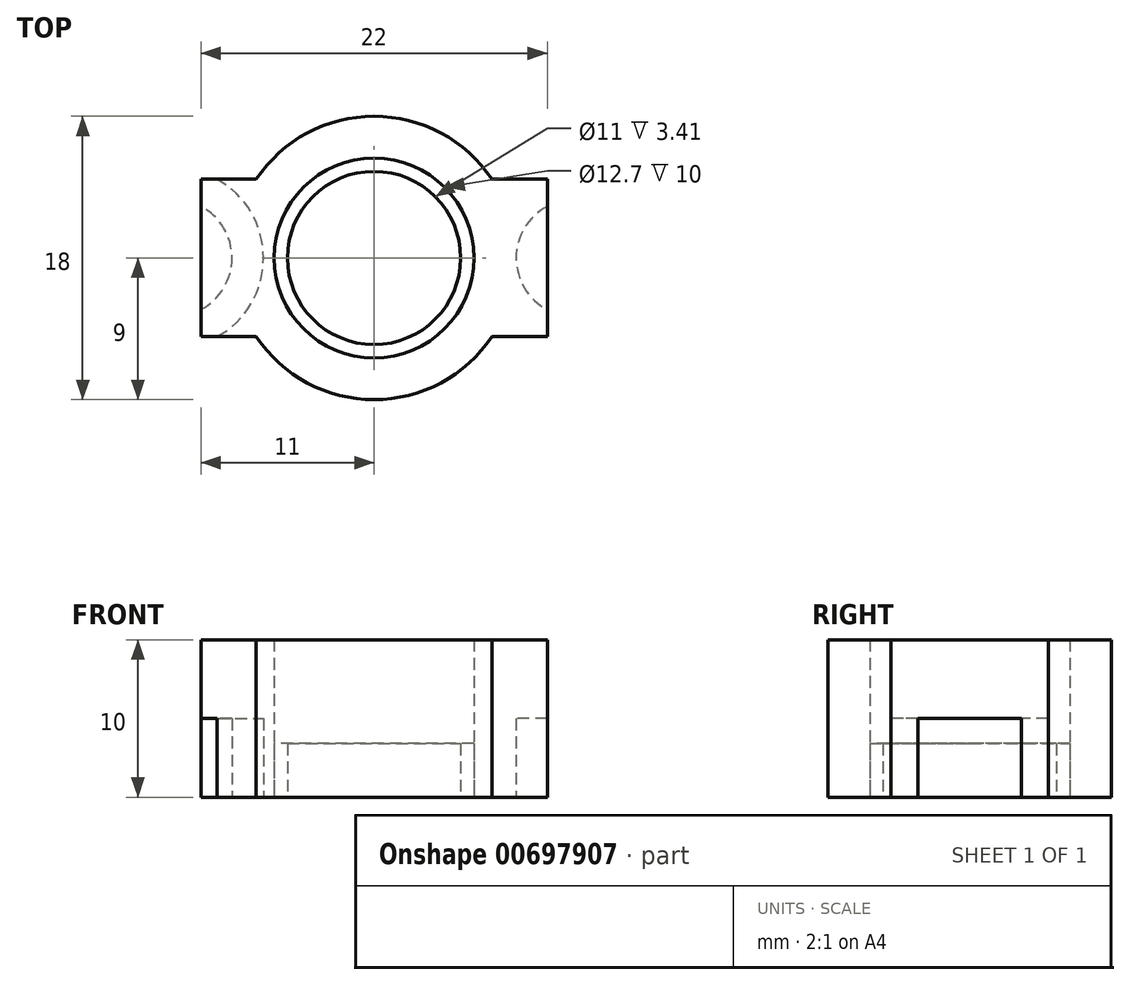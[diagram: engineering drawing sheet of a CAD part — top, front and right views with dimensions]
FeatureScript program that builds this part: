
annotation { "Feature Type Name" : "Feature", "Feature Type Description" : "" }
export const myFeature = defineFeature(function(context is Context, id is Id, definition is map)
    precondition{}
    {
        {
            var Q0;
            Q0=qCreatedBy(makeId("Top.planeOp"),FACE);
            var sketch = newSketch(context, id + "F0", { "sketchPlane" : qUnion([Q0])});
            skLineSegment(sketch, "E0", {"start": v(0, 0) * mm, "end": v(-38, 0) * mm, "construction": true});
            skLineSegment(sketch, "E1", {"start": v(0, 0) * mm, "end": v(38, 0) * mm, "construction": true});
            skCircle(sketch, "E2", {"center": v(0, 0) * mm, "radius": 6.35 * mm});
            skArc(sketch, "E3", {"start": v(-7.48, -5) * mm, "mid": v(0, -9) * mm, "end": v(7.48, -5) * mm});
            skLineSegment(sketch, "E4.bottom", {"start": v(-11, 5) * mm, "end": v(-7.48, 5) * mm});
            skLineSegment(sketch, "E4.top", {"start": v(-11, -5) * mm, "end": v(-7.48, -5) * mm});
            skLineSegment(sketch, "E4.left", {"start": v(-11, 5) * mm, "end": v(-11, -5) * mm});
            skLineSegment(sketch, "E4.right", {"start": v(11, 5) * mm, "end": v(11, -5) * mm});
            skLineSegment(sketch, "E5.trimOffspring", {"start": v(7.48, -5) * mm, "end": v(11, -5) * mm});
            skLineSegment(sketch, "E6.trimOffspring", {"start": v(7.48, 5) * mm, "end": v(11, 5) * mm});
            skArc(sketch, "E7.trimOffspring", {"start": v(7.48, 5) * mm, "mid": v(0, 9) * mm, "end": v(-7.48, 5) * mm});
            skSolve(sketch);
        }
        {
            var Q0;
            Q0=makeQuery(id+"F0.imprint","IMPRINT",FACE,{"disambiguationData":[TD([[makeQuery(id+"F0.imprint","IMPRINT",EDGE,{"derivedFrom":sQuery(id+"F0.wireOp",EDGE,"E2")}),-1.0]])]});
            extrude(context, id + "F1", {"entities" : qUnion([Q0]), "endBound" : BoundingType.SYMMETRIC, "depth" : 10 * mm, "offsetDistance" : 25 * mm});
        }
        {
            var Q0;
            Q0=makeQuery(id+"F1.opExtrude","CAP_FACE",FACE,{"disambiguationData":[OSD([sQuery(id+"F0.wireOp",EDGE,"E2"),sQuery(id+"F0.wireOp",EDGE,"E3"),sQuery(id+"F0.wireOp",EDGE,"E4.bottom"),sQuery(id+"F0.wireOp",EDGE,"E4.top"),sQuery(id+"F0.wireOp",EDGE,"E4.left"),sQuery(id+"F0.wireOp",EDGE,"E4.right"),sQuery(id+"F0.wireOp",EDGE,"E5.trimOffspring"),sQuery(id+"F0.wireOp",EDGE,"E6.trimOffspring"),sQuery(id+"F0.wireOp",EDGE,"E7.trimOffspring")])],"isStart":true});
            var sketch = newSketch(context, id + "F2", { "sketchPlane" : qUnion([Q0])});
            skArc(sketch, "E8", {"start": v(-11, -3.28) * mm, "mid": v(-9.02, 0) * mm, "end": v(-11, 3.28) * mm});
            skArc(sketch, "E9.0", {"start": v(-10.64, -5.32) * mm, "mid": v(-7.03, 0.2) * mm, "end": v(-11, 5.44) * mm});
            skLineSegment(sketch, "E10", {"start": v(0, 10.32) * mm, "end": v(0, -10.36) * mm, "construction": true});
            skArc(sketch, "E11.MirrorCS", {"start": v(10.64, -5.32) * mm, "mid": v(7.03, 0.2) * mm, "end": v(11, 5.44) * mm});
            skArc(sketch, "E12.MirrorCS", {"start": v(11, -3.28) * mm, "mid": v(9.02, 0) * mm, "end": v(11, 3.28) * mm});
            skSolve(sketch);
        }
        {
            var Q0;
            {var subQ0=sQuery(id+"F2.wireOp",EDGE,"E8");Q0=makeQuery(id+"F2.imprint","IMPRINT",FACE,{"disambiguationData":[TD([[makeQuery(id+"F2.imprint","IMPRINT",EDGE,{"derivedFrom":subQ0}),-1.0]])]});}
            var Q1;
            {var subQ4=sQuery(id+"F2.wireOp",EDGE,"E12.MirrorCS");Q1=makeQuery(id+"F2.imprint","IMPRINT",FACE,{"disambiguationData":[TD([[makeQuery(id+"F2.imprint","IMPRINT",EDGE,{"derivedFrom":subQ4}),1.0]])]});}
            extrude(context, id + "F3", {"entities" : qUnion([Q0, Q1]), "operationType" : NewBodyOperationType.REMOVE, "oppositeDirection" : true, "depth" : 5 * mm, "offsetDistance" : 25 * mm});
        }
        {
            var Q0;
            Q0=makeQuery(id+"F1.opExtrude","CAP_FACE",FACE,{"disambiguationData":[OSD([sQuery(id+"F0.wireOp",EDGE,"E2"),sQuery(id+"F0.wireOp",EDGE,"E3"),sQuery(id+"F0.wireOp",EDGE,"E4.bottom"),sQuery(id+"F0.wireOp",EDGE,"E4.top"),sQuery(id+"F0.wireOp",EDGE,"E4.left"),sQuery(id+"F0.wireOp",EDGE,"E4.right"),sQuery(id+"F0.wireOp",EDGE,"E5.trimOffspring"),sQuery(id+"F0.wireOp",EDGE,"E6.trimOffspring"),sQuery(id+"F0.wireOp",EDGE,"E7.trimOffspring")])],"isStart":false});
            var sketch = newSketch(context, id + "F4", { "sketchPlane" : qUnion([Q0])});
            skLineSegment(sketch, "E13", {"start": v(-3.67, 8.22) * mm, "end": v(3.67, 8.22) * mm});
            skLineSegment(sketch, "E14", {"start": v(-10.62, 0) * mm, "end": v(11.37, 0) * mm, "construction": true});
            skLineSegment(sketch, "E15.MirrorCS", {"start": v(-3.67, -8.22) * mm, "end": v(3.67, -8.22) * mm});
            skSolve(sketch);
        }
        {
            var Q0;
            {var subQ0=sQuery(id+"F4.wireOp",EDGE,"E13");Q0=makeQuery(id+"F4.imprint","IMPRINT",FACE,{"disambiguationData":[TD([[makeQuery(id+"F4.imprint","IMPRINT",EDGE,{"derivedFrom":subQ0}),1.0]])]});}
            var Q1;
            {var subQ0=sQuery(id+"F4.wireOp",EDGE,"E15.MirrorCS");Q1=makeQuery(id+"F4.imprint","IMPRINT",FACE,{"disambiguationData":[TD([[makeQuery(id+"F4.imprint","IMPRINT",EDGE,{"derivedFrom":subQ0}),-1.0]])]});}
            extrude(context, id + "F5", {"entities" : qUnion([Q0, Q1]), "operationType" : NewBodyOperationType.REMOVE, "depth" : 25 * mm, "offsetDistance" : 25 * mm});
        }
        {
            var Q0;
            {var subQ0=sQuery(id+"F0.wireOp",EDGE,"E4.bottom");var subQ1=sQuery(id+"F0.wireOp",EDGE,"E3");var subQ2=sQuery(id+"F0.wireOp",EDGE,"E4.top");var subQ3=sQuery(id+"F0.wireOp",EDGE,"E2");var subQ4=sQuery(id+"F0.wireOp",EDGE,"E5.trimOffspring");var subQ5=sQuery(id+"F0.wireOp",EDGE,"E6.trimOffspring");var subQ6=sQuery(id+"F0.wireOp",EDGE,"E7.trimOffspring");Q0=makeQuery(id+"F3.boolean.opBoolean","SPLIT",FACE,{"disambiguationData":[TD([makeQuery(id+"F1.opExtrude","SWEPT_FACE",FACE,{"disambiguationData":[OSD([subQ3])]})])],"derivedFrom":makeQuery(id+"F1.opExtrude","CAP_FACE",FACE,{"disambiguationData":[OSD([subQ3,subQ1,subQ0,subQ2,sQuery(id+"F0.wireOp",EDGE,"E4.left"),sQuery(id+"F0.wireOp",EDGE,"E4.right"),subQ4,subQ5,subQ6])],"isStart":true})});}
            var sketch = newSketch(context, id + "F6", { "sketchPlane" : qUnion([Q0])});
            skCircle(sketch, "E16", {"center": v(0, 0) * mm, "radius": 5.5 * mm});
            skSolve(sketch);
        }
        {
            var Q0;
            Q0=makeQuery(id+"F6.imprint","IMPRINT",FACE,{"disambiguationData":[TD([[makeQuery(id+"F6.imprint","IMPRINT",EDGE,{"derivedFrom":sQuery(id+"F6.wireOp",EDGE,"E16")}),-1.0]])]});
            extrude(context, id + "F7", {"entities" : qUnion([Q0]), "oppositeDirection" : true, "depth" : 3.41 * mm, "offsetDistance" : 25 * mm});
        }
    });
